# Revit family: Fire_Extinguisher_Cabinet-Strike_First-Centurion_Stand
name_source: partatom
category: Specialty Equipment
revit_build: Autodesk Revit Architecture 2013 (Build: 20130531_2115(x64)
units: mm (PartAtom-declared; Revit-internal decimal feet)

## types (2) — shared parameters
Assembly Code = D4030200
Cabinet Finish = Plastic-Strike_First-Red
Description = Portable Fire Extinguisher Stand
Finish = Plastic-Strike_First-Yellow
Glass = Glass-Strike_First-Acrylic
Manufacturer = Strike First Corporation of America
Product Documentation Link = http://www.strikefirstusa.com
Product Name = the CENTURION Portable Fire Extinguisher Stand
Product Page URL = http://www.strikefirstusa.com
Specification = http://www.strikefirstusa.com
Style = Portable
URL = http://www.strikefirstusa.com

## per-type parameters (varying)
| type | 10 lb Cabinet | 20 lb Cabinet | Bottom Tub Offset | Depth | Height | Model | Outer Tub Width | Support Thickness | Tub Back Offset | Type Comments | Width |
| 10 lb Fire Extinguisher Stand | Yes | No | 2' - 1 7/8" | 1' - 5 1/2" | 3' - 9 3/4" | CENTURION-10 | 0' - 7 3/4" | 0' - 4" | 0' - 4 13/16" | 10 lb Cabinet | 1' - 10" |
| 20 lb Fire Extinguisher Stand | No | Yes | 2' - 7 1/4" | 1' - 9" | 4' - 8" | CENTURION-20 | 0' - 10" | 0' - 6" | 0' - 7 1/16" | 20 lb Cabinet | 2' - 3 1/2" |

## geometry (parser evidence)
native form markers: Blend x10, Sweep x5
no freeform markers — native parametric forms only
